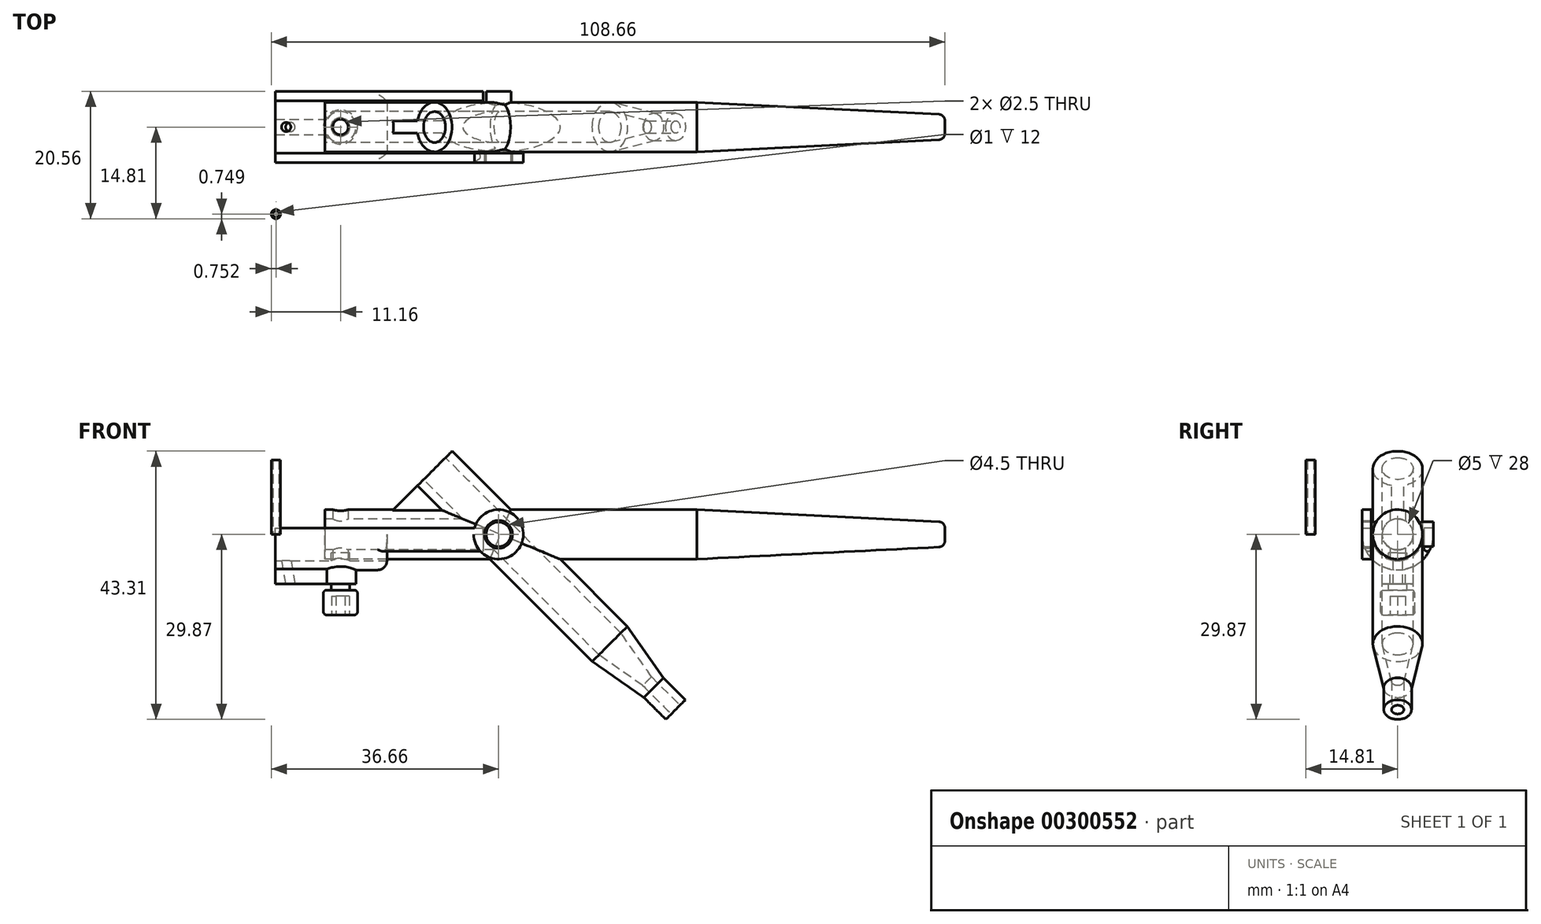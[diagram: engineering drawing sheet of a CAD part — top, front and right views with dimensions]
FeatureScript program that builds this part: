
annotation { "Feature Type Name" : "Feature", "Feature Type Description" : "" }
export const myFeature = defineFeature(function(context is Context, id is Id, definition is map)
    precondition{}
    {
        {
            var Q0;
            Q0=qCreatedBy(makeId("Right.planeOp"),FACE);
            var sketch = newSketch(context, id + "F0", { "sketchPlane" : qUnion([Q0])});
            skCircle(sketch, "E0", {"center": v(0, 0) * mm, "radius": 4 * mm});
            skSolve(sketch);
        }
        {
            var Q0;
            Q0 = qSketchRegion(id + "F0", true);
            extrude(context, id + "F1", {"entities" : qUnion([Q0]), "depth" : 100 * mm});
        }
        {
            var Q0;
            Q0=makeQuery(id+"F1.opExtrude","CAP_EDGE",EDGE,{"disambiguationData":[OSD([sQuery(id+"F0.wireOp",EDGE,"E0")])],"isStart":false});
            chamfer(context, id + "F2", {"entities" : qUnion([Q0]), "chamferType" : ChamferType.TWO_OFFSETS, "width1" : 2 * mm, "oppositeDirection" : false, "width2" : 40 * mm, "tangentPropagation" : true});
        }
        {
            var Q0;
            Q0=makeQuery(id+"F1.opExtrude","CAP_FACE",FACE,{"disambiguationData":[OSD([sQuery(id+"F0.wireOp",EDGE,"E0")])],"isStart":true});
            var sketch = newSketch(context, id + "F3", { "sketchPlane" : qUnion([Q0])});
            skCircle(sketch, "E1", {"center": v(0, 0) * mm, "radius": 2.5 * mm});
            skSolve(sketch);
        }
        {
            var Q0;
            Q0=qCreatedBy(makeId("Top.planeOp"),FACE);
            var Q1;
            Q1=qCreatedBy(makeId("Right.planeOp"),FACE);
            cPlane(context, id + "F4", {"entities" : qUnion([Q0, Q1]), "cplaneType" : CPlaneType.MID_PLANE, "offset" : 25 * mm, "width" : 150 * mm, "height" : 150 * mm});
        }
        {
            var Q0;
            Q0=qCreatedBy(id+"F4.planeOp",FACE);
            var sketch = newSketch(context, id + "F5", { "sketchPlane" : qUnion([Q0])});
            skCircle(sketch, "E2", {"center": v(0, 20) * mm, "radius": 4 * mm});
            skSolve(sketch);
        }
        {
            var Q0;
            Q0 = qSketchRegion(id + "F5", true);
            extrude(context, id + "F6", {"entities" : qUnion([Q0]), "operationType" : NewBodyOperationType.ADD, "oppositeDirection" : true, "depth" : 45 * mm, "hasSecondDirection" : true, "secondDirectionOppositeDirection" : true, "secondDirectionDepth" : 5 * mm});
        }
        {
            var Q0;
            Q0=makeQuery(id+"F6.opExtrude","CAP_FACE",FACE,{"disambiguationData":[OSD([sQuery(id+"F5.wireOp",EDGE,"E2")])],"isStart":true});
            var sketch = newSketch(context, id + "F7", { "sketchPlane" : qUnion([Q0])});
            skCircle(sketch, "E3", {"center": v(0, 20) * mm, "radius": 2.5 * mm});
            skSolve(sketch);
        }
        {
            var Q0;
            Q0=qCreatedBy(makeId("Front.planeOp"),FACE);
            var sketch = newSketch(context, id + "F8", { "sketchPlane" : qUnion([Q0])});
            skCircle(sketch, "E4", {"center": v(28, 0) * mm, "radius": 2 * mm});
            skSolve(sketch);
        }
        {
            var Q0;
            Q0 = qSketchRegion(id + "F8", true);
            extrude(context, id + "F9", {"entities" : qUnion([Q0]), "operationType" : NewBodyOperationType.ADD, "endBound" : BoundingType.SYMMETRIC, "depth" : 11.5 * mm, "hasSecondDirection" : true, "secondDirectionOppositeDirection" : true, "secondDirectionDepth" : 25 * mm});
        }
        {
            var Q0;
            Q0 = qSketchRegion(id + "F7", true);
            extrude(context, id + "F10", {"entities" : qUnion([Q0]), "operationType" : NewBodyOperationType.REMOVE, "endBound" : BoundingType.THROUGH_ALL, "oppositeDirection" : true, "depth" : 25 * mm});
        }
        {
            var Q0;
            Q0=makeQuery(id+"F6.opExtrude","CAP_FACE",FACE,{"disambiguationData":[OSD([sQuery(id+"F5.wireOp",EDGE,"E2")])],"isStart":false});
            var sketch = newSketch(context, id + "F11", { "sketchPlane" : qUnion([Q0])});
            skCircle(sketch, "E5.0", {"center": v(0, 20) * mm, "radius": 4 * mm});
            skSolve(sketch);
        }
        {
            var Q0;
            Q0 = qSketchRegion(id + "F11", true);
            extrude(context, id + "F12", {"entities" : qUnion([Q0]), "operationType" : NewBodyOperationType.ADD, "depth" : 10 * mm, "hasDraft" : true, "draftAngle" : 10 * degree, "draftPullDirection" : true});
        }
        {
            var Q0;
            Q0=makeQuery(id+"F12.opExtrude","CAP_FACE",FACE,{"disambiguationData":[OSD([sQuery(id+"F11.wireOp",EDGE,"E5.0")])],"isStart":true});
            extrude(context, id + "F13", {"entities" : qUnion([Q0]), "operationType" : NewBodyOperationType.REMOVE, "oppositeDirection" : true, "depth" : 25 * mm, "hasDraft" : true, "draftAngle" : 10 * degree, "draftPullDirection" : true});
        }
        {
            var Q0;
            Q0=makeQuery(id+"F12.opExtrude","CAP_FACE",FACE,{"disambiguationData":[OSD([sQuery(id+"F11.wireOp",EDGE,"E5.0")])],"isStart":false});
            extrude(context, id + "F14", {"entities" : qUnion([Q0]), "operationType" : NewBodyOperationType.ADD, "depth" : 5 * mm});
        }
        {
            var Q0;
            Q0=makeQuery(id+"F14.opExtrude","CAP_FACE",FACE,{"disambiguationData":[OSD([sQuery(id+"F11.wireOp",EDGE,"E5.0")])],"isStart":false});
            var sketch = newSketch(context, id + "F15", { "sketchPlane" : qUnion([Q0])});
            skCircle(sketch, "E6", {"center": v(0, 20) * mm, "radius": 1 * mm});
            skSolve(sketch);
        }
        {
            var Q0;
            Q0 = qSketchRegion(id + "F15", true);
            extrude(context, id + "F16", {"entities" : qUnion([Q0]), "operationType" : NewBodyOperationType.REMOVE, "endBound" : BoundingType.THROUGH_ALL, "oppositeDirection" : true, "depth" : 25 * mm});
        }
        {
            var Q0;
            Q0=makeQuery(id+"F6.opExtrude","CAP_FACE",FACE,{"disambiguationData":[OSD([sQuery(id+"F5.wireOp",EDGE,"E2")])],"isStart":true});
            var sketch = newSketch(context, id + "F17", { "sketchPlane" : qUnion([Q0])});
            skLineSegment(sketch, "E7.bottom", {"start": v(1, 10) * mm, "end": v(-1, 10) * mm});
            skLineSegment(sketch, "E7.top", {"start": v(1, 17) * mm, "end": v(-1, 17) * mm});
            skLineSegment(sketch, "E7.left", {"start": v(1, 10) * mm, "end": v(1, 17) * mm});
            skLineSegment(sketch, "E7.right", {"start": v(-1, 10) * mm, "end": v(-1, 17) * mm});
            skPoint(sketch, "E7.middle", {"position": v(0, 0) * mm});
            skSolve(sketch);
        }
        {
            var Q0;
            Q0 = qSketchRegion(id + "F17", true);
            var Q1;
            {var subQ0=sQuery(id+"F0.wireOp",EDGE,"E0");var subQ1=makeQuery(id+"F1.opExtrude","SWEPT_FACE",FACE,{"disambiguationData":[OSD([subQ0])]});Q1=makeQuery(id+"F6.boolean.opBoolean","SPLIT",FACE,{"disambiguationData":[TD([makeQuery(id+"F1.opExtrude","CAP_FACE",FACE,{"disambiguationData":[OSD([subQ0])],"isStart":true})])],"derivedFrom":subQ1});}
            extrude(context, id + "F18", {"entities" : qUnion([Q0]), "operationType" : NewBodyOperationType.ADD, "oppositeDirection" : true, "endBoundEntityFace" : qUnion([Q1]), "depth" : 6 * mm});
        }
        {
            var Q0;
            Q0 = qSketchRegion(id + "F3", true);
            extrude(context, id + "F19", {"entities" : qUnion([Q0]), "operationType" : NewBodyOperationType.REMOVE, "oppositeDirection" : true, "depth" : 28 * mm});
        }
        {
            var Q0;
            Q0=makeQuery(id+"F1.opExtrude","CAP_FACE",FACE,{"disambiguationData":[OSD([sQuery(id+"F0.wireOp",EDGE,"E0")])],"isStart":true});
            var sketch = newSketch(context, id + "F20", { "sketchPlane" : qUnion([Q0])});
            skArc(sketch, "E8", {"start": v(4.25, 0) * mm, "mid": v(0, -4.25) * mm, "end": v(-4.25, 0) * mm});
            skArc(sketch, "E9", {"start": v(5.75, 0) * mm, "mid": v(0, -5.75) * mm, "end": v(-5.75, 0) * mm});
            skLineSegment(sketch, "E10", {"start": v(-5.75, 0) * mm, "end": v(-5.75, 1) * mm});
            skLineSegment(sketch, "E11", {"start": v(-5.75, 1) * mm, "end": v(-4.25, 1) * mm});
            skLineSegment(sketch, "E12", {"start": v(-4.25, 1) * mm, "end": v(-4.25, 0) * mm});
            skLineSegment(sketch, "E13", {"start": v(4.25, 0) * mm, "end": v(4.25, 1) * mm});
            skLineSegment(sketch, "E14", {"start": v(4.25, 1) * mm, "end": v(5.75, 1) * mm});
            skLineSegment(sketch, "E15", {"start": v(5.75, 1) * mm, "end": v(5.75, 0) * mm});
            skSolve(sketch);
        }
        {
            var Q0;
            Q0 = qSketchRegion(id + "F20", true);
            extrude(context, id + "F21", {"entities" : qUnion([Q0]), "depth" : 8 * mm, "hasSecondDirection" : true, "secondDirectionOppositeDirection" : true, "secondDirectionDepth" : 10 * mm});
        }
        {
            var Q0;
            Q0=makeQuery(id+"F21.opExtrude","CAP_FACE",FACE,{"disambiguationData":[OSD([sQuery(id+"F20.wireOp",EDGE,"E8"),sQuery(id+"F20.wireOp",EDGE,"E9"),sQuery(id+"F20.wireOp",EDGE,"E10"),sQuery(id+"F20.wireOp",EDGE,"E11"),sQuery(id+"F20.wireOp",EDGE,"E12"),sQuery(id+"F20.wireOp",EDGE,"E13"),sQuery(id+"F20.wireOp",EDGE,"E14"),sQuery(id+"F20.wireOp",EDGE,"E15")])],"isStart":true});
            var sketch = newSketch(context, id + "F22", { "sketchPlane" : qUnion([Q0])});
            skLineSegment(sketch, "E16", {"start": v(4.25, 1) * mm, "end": v(4.25, -3.87) * mm});
            skLineSegment(sketch, "E17", {"start": v(-4.25, 1) * mm, "end": v(-4.25, -3.87) * mm});
            skSolve(sketch);
        }
        {
            var Q0;
            {var subQ3=makeQuery(id+"F21.opExtrude","CAP_EDGE",EDGE,{"disambiguationData":[OSD([sQuery(id+"F20.wireOp",EDGE,"E10")])],"isStart":true});Q0=makeQuery(id+"F22.imprint","IMPRINT",FACE,{"disambiguationData":[TD([[makeQuery(id+"F22.imprint","IMPRINT",EDGE,{"derivedFrom":subQ3}),1.0]])]});}
            var Q1;
            {var subQ3=makeQuery(id+"F21.opExtrude","CAP_EDGE",EDGE,{"disambiguationData":[OSD([sQuery(id+"F20.wireOp",EDGE,"E14")])],"isStart":true});Q1=makeQuery(id+"F22.imprint","IMPRINT",FACE,{"disambiguationData":[TD([[makeQuery(id+"F22.imprint","IMPRINT",EDGE,{"derivedFrom":subQ3}),1.0]])]});}
            extrude(context, id + "F23", {"entities" : qUnion([Q0, Q1]), "operationType" : NewBodyOperationType.ADD, "depth" : 15.5 * mm});
        }
        {
            var Q0;
            Q0=makeQuery(id+"F21.opExtrude","CAP_EDGE",EDGE,{"disambiguationData":[OSD([sQuery(id+"F20.wireOp",EDGE,"E9")])],"isStart":true});
            fillet(context, id + "F24", {"entities" : qUnion([Q0]), "radius" : 1.5 * mm, "tangentPropagation" : true, "allowEdgeOverflow" : false});
        }
        {
            var Q0;
            Q0=makeQuery(id+"F23.opExtrude","SWEPT_EDGE",EDGE,{"disambiguationData":[OSD([sQuery(id+"F20.wireOp",EDGE,"E9"),sQuery(id+"F22.wireOp",EDGE,"E17")])]});
            var Q1;
            Q1=makeQuery(id+"F23.opExtrude","SWEPT_EDGE",EDGE,{"disambiguationData":[OSD([sQuery(id+"F20.wireOp",EDGE,"E9"),sQuery(id+"F22.wireOp",EDGE,"E16")])]});
            fillet(context, id + "F25", {"entities" : qUnion([Q0, Q1]), "radius" : 0.5 * mm, "tangentPropagation" : true, "allowEdgeOverflow" : false});
        }
        {
            var Q0;
            Q0=makeQuery(id+"F23.boolean.opBoolean","MERGE",FACE,{"derivedFrom":[makeQuery(id+"F21.opExtrude","SWEPT_FACE",FACE,{"disambiguationData":[OSD([sQuery(id+"F20.wireOp",EDGE,"E13")])]}),makeQuery(id+"F23.opExtrude","SWEPT_FACE",FACE,{"disambiguationData":[OSD([sQuery(id+"F22.wireOp",EDGE,"E17")])]})]});
            var sketch = newSketch(context, id + "F26", { "sketchPlane" : qUnion([Q0])});
            skCircle(sketch, "E18", {"center": v(-28, 0) * mm, "radius": 2.25 * mm});
            skCircle(sketch, "E19", {"center": v(-28, 0) * mm, "radius": 4 * mm});
            skSolve(sketch);
        }
        {
            var Q0;
            Q0 = qSketchRegion(id + "F26", true);
            extrude(context, id + "F27", {"entities" : qUnion([Q0]), "operationType" : NewBodyOperationType.ADD, "oppositeDirection" : true, "depth" : 1.5 * mm});
        }
        {
            var Q0;
            Q0=qCreatedBy(makeId("Top.planeOp"),FACE);
            var sketch = newSketch(context, id + "F28", { "sketchPlane" : qUnion([Q0])});
            skCircle(sketch, "E20", {"center": v(2.5, 0) * mm, "radius": 2.5 * mm});
            skSolve(sketch);
        }
        {
            var Q0;
            Q0 = qSketchRegion(id + "F28", true);
            extrude(context, id + "F29", {"entities" : qUnion([Q0]), "operationType" : NewBodyOperationType.ADD, "oppositeDirection" : true, "depth" : 8 * mm, "hasSecondDirection" : true, "secondDirectionOppositeDirection" : true, "secondDirectionDepth" : 5 * mm});
        }
        {
            var Q0;
            Q0=makeQuery(id+"F29.opExtrude","CAP_FACE",FACE,{"disambiguationData":[OSD([sQuery(id+"F28.wireOp",EDGE,"E20")])],"isStart":false});
            var sketch = newSketch(context, id + "F30", { "sketchPlane" : qUnion([Q0])});
            skCircle(sketch, "E21", {"center": v(2.5, 0) * mm, "radius": 1.25 * mm});
            skSolve(sketch);
        }
        {
            var Q0;
            Q0 = qSketchRegion(id + "F30", true);
            extrude(context, id + "F31", {"entities" : qUnion([Q0]), "operationType" : NewBodyOperationType.REMOVE, "endBound" : BoundingType.THROUGH_ALL, "oppositeDirection" : true, "depth" : 25 * mm});
        }
        {
            var Q0;
            Q0=makeQuery(id+"F29.opExtrude","CAP_FACE",FACE,{"disambiguationData":[OSD([sQuery(id+"F28.wireOp",EDGE,"E20")])],"isStart":false});
            var sketch = newSketch(context, id + "F32", { "sketchPlane" : qUnion([Q0])});
            skCircle(sketch, "E22", {"center": v(2.5, 0) * mm, "radius": 1.5 * mm});
            skSolve(sketch);
        }
        {
            var Q0;
            Q0 = qSketchRegion(id + "F32", true);
            extrude(context, id + "F33", {"entities" : qUnion([Q0]), "depth" : 1 * mm, "hasSecondDirection" : true, "secondDirectionOppositeDirection" : true, "secondDirectionDepth" : 5 * mm});
        }
        {
            var Q0;
            Q0=makeQuery(id+"F33.opExtrude","CAP_FACE",FACE,{"disambiguationData":[OSD([sQuery(id+"F32.wireOp",EDGE,"E22")])],"isStart":false});
            var sketch = newSketch(context, id + "F34", { "sketchPlane" : qUnion([Q0])});
            skCircle(sketch, "E23", {"center": v(2.5, 0) * mm, "radius": 2.75 * mm});
            skSolve(sketch);
        }
        {
            var Q0;
            Q0 = qSketchRegion(id + "F34", true);
            extrude(context, id + "F35", {"entities" : qUnion([Q0]), "operationType" : NewBodyOperationType.ADD, "depth" : 4 * mm});
        }
        {
            var Q0;
            Q0=makeQuery(id+"F35.opExtrude","SWEPT_FACE",FACE,{"disambiguationData":[OSD([sQuery(id+"F34.wireOp",EDGE,"E23")])]});
            fillet(context, id + "F36", {"entities" : qUnion([Q0]), "radius" : .5 * mm, "tangentPropagation" : true, "allowEdgeOverflow" : false});
        }
        {
            var Q0;
            Q0=makeQuery(id+"F35.opExtrude","CAP_FACE",FACE,{"disambiguationData":[OSD([sQuery(id+"F34.wireOp",EDGE,"E23")])],"isStart":false});
            var sketch = newSketch(context, id + "F37", { "sketchPlane" : qUnion([Q0])});
            skCircle(sketch, "E24.cCircle", {"center": v(2.5, 0) * mm, "radius": 1.25 * mm, "construction": true});
            skLineSegment(sketch, "E24.0", {"start": v(3.22, -1.25) * mm, "end": v(1.78, -1.25) * mm});
            skLineSegment(sketch, "E24.1", {"start": v(1.78, -1.25) * mm, "end": v(1.06, 0) * mm});
            skLineSegment(sketch, "E24.2", {"start": v(1.06, 0) * mm, "end": v(1.78, 1.25) * mm});
            skLineSegment(sketch, "E24.3", {"start": v(1.78, 1.25) * mm, "end": v(3.22, 1.25) * mm});
            skLineSegment(sketch, "E24.4", {"start": v(3.22, 1.25) * mm, "end": v(3.94, 0) * mm});
            skLineSegment(sketch, "E24.5", {"start": v(3.94, 0) * mm, "end": v(3.22, -1.25) * mm});
            skPoint(sketch, "E24.0.midPoint", {"position": v(2.5, -1.25) * mm});
            skSolve(sketch);
        }
        {
            var Q0;
            Q0=makeQuery(id+"F21.opExtrude","CAP_FACE",FACE,{"disambiguationData":[OSD([sQuery(id+"F20.wireOp",EDGE,"E8"),sQuery(id+"F20.wireOp",EDGE,"E9"),sQuery(id+"F20.wireOp",EDGE,"E10"),sQuery(id+"F20.wireOp",EDGE,"E11"),sQuery(id+"F20.wireOp",EDGE,"E12"),sQuery(id+"F20.wireOp",EDGE,"E13"),sQuery(id+"F20.wireOp",EDGE,"E14"),sQuery(id+"F20.wireOp",EDGE,"E15")])],"isStart":false});
            var sketch = newSketch(context, id + "F38", { "sketchPlane" : qUnion([Q0])});
            skLineSegment(sketch, "E25.bottom", {"start": v(1.25, -8) * mm, "end": v(-1.25, -8) * mm});
            skLineSegment(sketch, "E25.top", {"start": v(1.25, -4.75) * mm, "end": v(-1.25, -4.75) * mm});
            skLineSegment(sketch, "E25.left", {"start": v(1.25, -8) * mm, "end": v(1.25, -4.75) * mm});
            skLineSegment(sketch, "E25.right", {"start": v(-1.25, -8) * mm, "end": v(-1.25, -4.75) * mm});
            skPoint(sketch, "E25.middle", {"position": v(0, -6.38) * mm});
            skPoint(sketch, "E25.centerSnap0", {"position": v(0, -5.75) * mm});
            skSolve(sketch);
        }
        {
            var Q0;
            Q0 = qSketchRegion(id + "F38", true);
            extrude(context, id + "F39", {"entities" : qUnion([Q0]), "operationType" : NewBodyOperationType.ADD, "oppositeDirection" : true, "depth" : 9 * mm});
        }
        {
            var Q0;
            Q0 = qSketchRegion(id + "F37", true);
            extrude(context, id + "F40", {"entities" : qUnion([Q0]), "operationType" : NewBodyOperationType.REMOVE, "oppositeDirection" : true, "depth" : 3 * mm});
        }
        {
            var Q0;
            Q0=qCreatedBy(makeId("Front.planeOp"),FACE);
            var sketch = newSketch(context, id + "F41", { "sketchPlane" : qUnion([Q0])});
            skLineSegment(sketch, "E26", {"start": v(0, 0) * mm, "end": v(-21, 0) * mm, "construction": true});
            skLineSegment(sketch, "E27.bottom", {"start": v(-7, 0) * mm, "end": v(-6.26, 0.13) * mm});
            skLineSegment(sketch, "E27.top", {"start": v(-5.18, -10.34) * mm, "end": v(-4.44, -10.2) * mm});
            skLineSegment(sketch, "E27.left", {"start": v(-7, 0) * mm, "end": v(-5.18, -10.34) * mm});
            skLineSegment(sketch, "E27.right", {"start": v(-6.26, 0.13) * mm, "end": v(-4.44, -10.2) * mm});
            skSolve(sketch);
        }
        {
            var Q0;
            Q0 = qSketchRegion(id + "F41", true);
            var Q1;
            Q1=sQuery(id+"F41.wireOp",EDGE,"E27.left");
            revolve(context, id + "F42", {"operationType" : NewBodyOperationType.REMOVE, "entities" : qUnion([Q0]), "axis" : qUnion([Q1]), "revolveType" : RevolveType.FULL, "oppositeDirection" : true});
        }
        {
            var Q0;
            Q0=qCreatedBy(makeId("Top.planeOp"),FACE);
            var sketch = newSketch(context, id + "F43", { "sketchPlane" : qUnion([Q0])});
            skCircle(sketch, "E28", {"center": v(-7.9, -14.06) * mm, "radius": 0.75 * mm});
            skCircle(sketch, "E29", {"center": v(-7.9, -14.06) * mm, "radius": 0.5 * mm});
            skSolve(sketch);
        }
        {
            var Q0;
            Q0 = qSketchRegion(id + "F43", true);
            extrude(context, id + "F44", {"entities" : qUnion([Q0]), "depth" : 12 * mm});
        }
        {
            var Q0;
            Q0=makeQuery(id+"F1.opExtrude","CAP_FACE",FACE,{"disambiguationData":[OSD([sQuery(id+"F0.wireOp",EDGE,"E0")])],"isStart":false});
            fillet(context, id + "F45", {"entities" : qUnion([Q0]), "radius" : 1 * mm, "tangentPropagation" : true, "allowEdgeOverflow" : false});
        }
    });
